# Revit family: ET1G
name_source: partatom
category: Generic Models
revit_build: Autodesk Revit LT 2017 (Build: 20160225_1515(x64)
units: mm (PartAtom-declared; Revit-internal decimal feet)

## family parameters
Always vertical = No
Can host rebar = No
Cut with Voids When Loaded = No
Part Type = Normal
Room Calculation Point = No
Round Connector Dimension = Use Diameter
Shared = No
Work Plane-Based = Yes

## types (1)
- NBS Standard Parameters
    BIMObjectName = Metpro_Metprolibrary_Conduitfittings_Metalcomponents_Malleablecircularbox
    Default Elevation = 1219 mm
    Description = ET1G  20mm Terminal Extension Malleable Conduit Box
    DurationUnit = year
    Finish = Galvanised
    Keynote = Compliant to LU Standard 1-085
    ManufacturerName = Metpro Ltd
    ManufacturerURL = www.metpro.co.uk
    Material = Malleable Iron
    ModelReference = ET1G
    NBSDescription = Conduit Fittings
    NBSReference = 90-55-10/460
    NominalHeight = 28 mm  [stored 0.0918635 ft]
    NominalLength = 63 mm  [stored 0.206693 ft]
    NominalWidth = 63 mm  [stored 0.206693 ft]
    ProductInformation = www.metpro.co.uk/pdf/et1g.pdf
    Shape = Circular
    Size = 20mm
    Uniclass2 = Pr_65_70_11_20
    Version = 1
    WarrantyDurationUnit = 1 year
    Weight = 0.2064Kg

note: [stored X ft] marks values corroborated as IEEE doubles in the binary element streams (Revit-internal decimal feet)

## geometry (parser evidence)
native form markers: Sweep x2
no freeform markers — native parametric forms only
